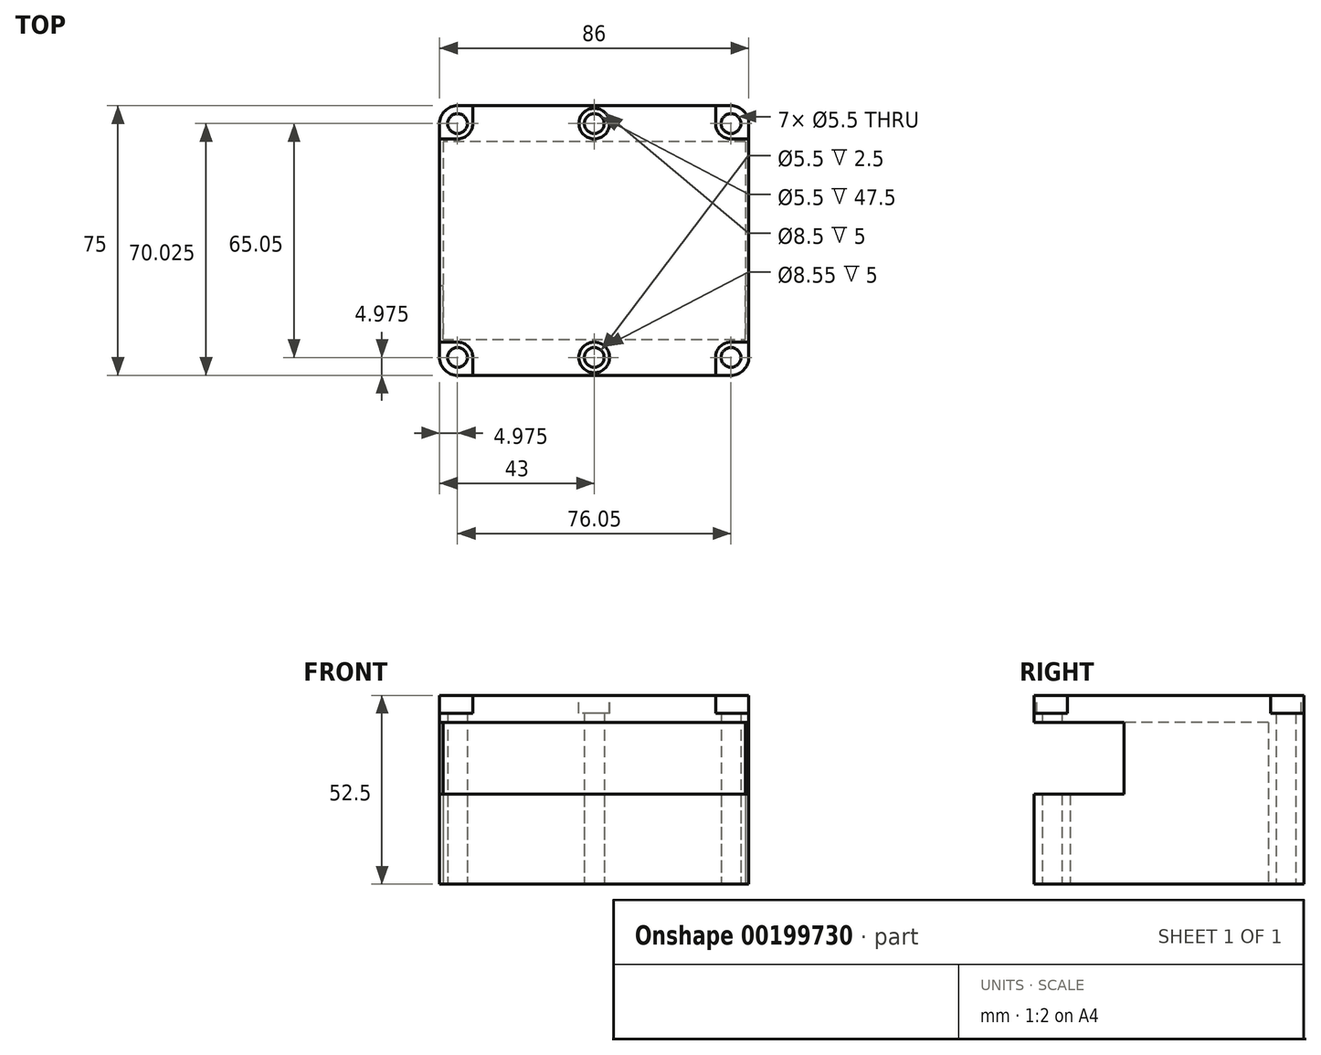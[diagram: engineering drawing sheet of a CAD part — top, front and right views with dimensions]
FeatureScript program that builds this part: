
annotation { "Feature Type Name" : "Feature", "Feature Type Description" : "" }
export const myFeature = defineFeature(function(context is Context, id is Id, definition is map)
    precondition{}
    {
        {
            var Q0;
            Q0=qCreatedBy(makeId("Top.planeOp"),FACE);
            var sketch = newSketch(context, id + "F0", { "sketchPlane" : qUnion([Q0])});
            skLineSegment(sketch, "E0.bottom", {"start": v(42.05, 27.55) * mm, "end": v(-42.05, 27.55) * mm});
            skLineSegment(sketch, "E0.top", {"start": v(42.05, -27.55) * mm, "end": v(-42.05, -27.55) * mm});
            skLineSegment(sketch, "E0.left", {"start": v(42.05, 27.55) * mm, "end": v(42.05, -27.55) * mm});
            skLineSegment(sketch, "E0.right", {"start": v(-42.05, 27.55) * mm, "end": v(-42.05, -27.55) * mm});
            skPoint(sketch, "E0.middle", {"position": v(0, 0) * mm});
            skLineSegment(sketch, "E1.bottom", {"start": v(43, 37.5) * mm, "end": v(-43, 37.5) * mm});
            skLineSegment(sketch, "E1.top", {"start": v(43, -37.5) * mm, "end": v(-43, -37.5) * mm});
            skLineSegment(sketch, "E1.left", {"start": v(43, 37.5) * mm, "end": v(43, -37.5) * mm});
            skLineSegment(sketch, "E1.right", {"start": v(-43, 37.5) * mm, "end": v(-43, -37.5) * mm});
            skSolve(sketch);
        }
        {
            var Q0;
            Q0=makeQuery(id+"F0.imprint","IMPRINT",FACE,{"disambiguationData":[TD([[makeQuery(id+"F0.imprint","IMPRINT",EDGE,{"derivedFrom":sQuery(id+"F0.wireOp",EDGE,"E0.bottom")}),-1.0]])]});
            extrude(context, id + "F1", {"entities" : qUnion([Q0]), "depth" : 45 * mm});
        }
        {
            var Q0;
            Q0=makeQuery(id+"F1.opExtrude","CAP_FACE",FACE,{"disambiguationData":[OSD([sQuery(id+"F0.wireOp",EDGE,"E0.bottom"),sQuery(id+"F0.wireOp",EDGE,"E0.top"),sQuery(id+"F0.wireOp",EDGE,"E0.left"),sQuery(id+"F0.wireOp",EDGE,"E0.right"),sQuery(id+"F0.wireOp",EDGE,"E1.bottom"),sQuery(id+"F0.wireOp",EDGE,"E1.top"),sQuery(id+"F0.wireOp",EDGE,"E1.left"),sQuery(id+"F0.wireOp",EDGE,"E1.right")])],"isStart":false});
            var sketch = newSketch(context, id + "F2", { "sketchPlane" : qUnion([Q0])});
            skLineSegment(sketch, "E2.0.0", {"start": v(43, -37.5) * mm, "end": v(43, 37.5) * mm});
            skLineSegment(sketch, "E2.0.1", {"start": v(43, 37.5) * mm, "end": v(-43, 37.5) * mm});
            skLineSegment(sketch, "E2.0.2", {"start": v(-43, 37.5) * mm, "end": v(-43, -37.5) * mm});
            skLineSegment(sketch, "E2.0.3", {"start": v(-43, -37.5) * mm, "end": v(43, -37.5) * mm});
            skSolve(sketch);
        }
        {
            var Q0;
            Q0=makeQuery(id+"F2.imprint","IMPRINT",FACE,{"disambiguationData":[TD([[makeQuery(id+"F2.imprint","IMPRINT",EDGE,{"derivedFrom":sQuery(id+"F2.wireOp",EDGE,"E2.0.0")}),-1.0]])]});
            var Q1;
            Q1=makeQuery(id+"F2.imprint","IMPRINT",FACE,{"disambiguationData":[TD([[makeQuery(id+"F2.imprint","IMPRINT",EDGE,{"derivedFrom":makeQuery(id+"F1.opExtrude","CAP_EDGE",EDGE,{"disambiguationData":[OSD([sQuery(id+"F0.wireOp",EDGE,"E0.bottom")])],"isStart":false})}),1.0]])]});
            extrude(context, id + "F3", {"entities" : qUnion([Q0, Q1]), "operationType" : NewBodyOperationType.ADD, "depth" : 5 * mm});
        }
        {
            var Q0;
            Q0=makeQuery(id+"F3.boolean.opBoolean","MERGE",FACE,{"derivedFrom":[makeQuery(id+"F1.opExtrude","SWEPT_FACE",FACE,{"disambiguationData":[OSD([sQuery(id+"F0.wireOp",EDGE,"E1.top")])]}),makeQuery(id+"F3.opExtrude","SWEPT_FACE",FACE,{"disambiguationData":[OSD([sQuery(id+"F2.wireOp",EDGE,"E2.0.3")])]})]});
            var sketch = newSketch(context, id + "F4", { "sketchPlane" : qUnion([Q0])});
            skLineSegment(sketch, "E3.0.0", {"start": v(-43, 0) * mm, "end": v(43, 0) * mm});
            skLineSegment(sketch, "E3.0.1", {"start": v(43, 0) * mm, "end": v(43, 50) * mm});
            skLineSegment(sketch, "E3.0.2", {"start": v(43, 50) * mm, "end": v(-43, 50) * mm});
            skLineSegment(sketch, "E3.0.3", {"start": v(-43, 50) * mm, "end": v(-43, 0) * mm});
            skLineSegment(sketch, "E4.bottom", {"start": v(-43, 50) * mm, "end": v(43, 50) * mm});
            skLineSegment(sketch, "E4.top", {"start": v(-43, 25) * mm, "end": v(43, 25) * mm});
            skLineSegment(sketch, "E4.left", {"start": v(-43, 50) * mm, "end": v(-43, 25) * mm});
            skLineSegment(sketch, "E4.right", {"start": v(43, 50) * mm, "end": v(43, 25) * mm});
            skLineSegment(sketch, "E5.top", {"start": v(-43, 45) * mm, "end": v(43, 45) * mm});
            skLineSegment(sketch, "E5.left", {"start": v(-43, 50) * mm, "end": v(-43, 45) * mm});
            skLineSegment(sketch, "E5.right", {"start": v(43, 50) * mm, "end": v(43, 45) * mm});
            skLineSegment(sketch, "E6.bottom", {"start": v(-43, 45) * mm, "end": v(-37.05, 45) * mm});
            skLineSegment(sketch, "E6.top", {"start": v(-43, 25) * mm, "end": v(-37.05, 25) * mm});
            skLineSegment(sketch, "E6.left", {"start": v(-43, 45) * mm, "end": v(-43, 25) * mm});
            skLineSegment(sketch, "E6.right", {"start": v(-37.05, 45) * mm, "end": v(-37.05, 25) * mm});
            skLineSegment(sketch, "E7.bottom", {"start": v(-37.05, 45) * mm, "end": v(-12.05, 45) * mm});
            skLineSegment(sketch, "E7.top", {"start": v(-37.05, 25) * mm, "end": v(-12.05, 25) * mm});
            skLineSegment(sketch, "E7.right", {"start": v(-12.05, 45) * mm, "end": v(-12.05, 25) * mm});
            skLineSegment(sketch, "E8.bottom", {"start": v(-12.05, 45) * mm, "end": v(-10.05, 45) * mm});
            skLineSegment(sketch, "E8.top", {"start": v(-12.05, 25) * mm, "end": v(-10.05, 25) * mm});
            skLineSegment(sketch, "E8.right", {"start": v(-10.05, 45) * mm, "end": v(-10.05, 25) * mm});
            skLineSegment(sketch, "E9.bottom", {"start": v(43, 45) * mm, "end": v(35.95, 45) * mm});
            skLineSegment(sketch, "E9.top", {"start": v(43, 25) * mm, "end": v(35.95, 25) * mm});
            skLineSegment(sketch, "E9.left", {"start": v(43, 45) * mm, "end": v(43, 25) * mm});
            skLineSegment(sketch, "E9.right", {"start": v(35.95, 45) * mm, "end": v(35.95, 25) * mm});
            skSolve(sketch);
        }
        {
            var Q0;
            Q0=makeQuery(id+"F4.imprint","IMPRINT",FACE,{"disambiguationData":[TD([[makeQuery(id+"F4.imprint","IMPRINT",EDGE,{"derivedFrom":sQuery(id+"F4.wireOp",EDGE,"E7.bottom")}),-1.0]])]});
            var Q1;
            Q1=makeQuery(id+"F4.imprint","IMPRINT",FACE,{"disambiguationData":[TD([[makeQuery(id+"F4.imprint","IMPRINT",EDGE,{"derivedFrom":sQuery(id+"F4.wireOp",EDGE,"E4.top")}),1.0]])]});
            extrude(context, id + "F5", {"entities" : qUnion([Q0, Q1]), "operationType" : NewBodyOperationType.REMOVE, "oppositeDirection" : true, "depth" : 25 * mm});
        }
        {
            var Q0;
            Q0=makeQuery(id+"F1.opExtrude","CAP_FACE",FACE,{"disambiguationData":[OSD([sQuery(id+"F0.wireOp",EDGE,"E0.bottom"),sQuery(id+"F0.wireOp",EDGE,"E0.top"),sQuery(id+"F0.wireOp",EDGE,"E0.left"),sQuery(id+"F0.wireOp",EDGE,"E0.right"),sQuery(id+"F0.wireOp",EDGE,"E1.bottom"),sQuery(id+"F0.wireOp",EDGE,"E1.top"),sQuery(id+"F0.wireOp",EDGE,"E1.left"),sQuery(id+"F0.wireOp",EDGE,"E1.right")])],"isStart":true});
            var sketch = newSketch(context, id + "F6", { "sketchPlane" : qUnion([Q0])});
            skLineSegment(sketch, "E10.0.0", {"start": v(43, -37.5) * mm, "end": v(43, 37.5) * mm});
            skLineSegment(sketch, "E10.0.1", {"start": v(43, 37.5) * mm, "end": v(-43, 37.5) * mm});
            skLineSegment(sketch, "E10.0.2", {"start": v(-43, 37.5) * mm, "end": v(-43, -37.5) * mm});
            skLineSegment(sketch, "E10.0.3", {"start": v(-43, -37.5) * mm, "end": v(43, -37.5) * mm});
            skPoint(sketch, "E11", {"position": v(-38.03, -32.52) * mm});
            skPoint(sketch, "E12", {"position": v(38.02, -32.52) * mm});
            skPoint(sketch, "E13", {"position": v(38.03, 32.53) * mm});
            skPoint(sketch, "E14", {"position": v(-38.02, 32.53) * mm});
            skCircle(sketch, "E15", {"center": v(-38.02, 32.53) * mm, "radius": 2.75 * mm});
            skCircle(sketch, "E16", {"center": v(38.03, 32.53) * mm, "radius": 2.75 * mm});
            skCircle(sketch, "E17", {"center": v(-38.03, -32.52) * mm, "radius": 2.75 * mm});
            skCircle(sketch, "E18", {"center": v(38.02, -32.52) * mm, "radius": 2.75 * mm});
            skPoint(sketch, "E19", {"position": v(0, 32.53) * mm});
            skPoint(sketch, "E20", {"position": v(0, -32.52) * mm});
            skCircle(sketch, "E21", {"center": v(0, -32.52) * mm, "radius": 2.75 * mm});
            skCircle(sketch, "E22", {"center": v(0, 32.53) * mm, "radius": 2.75 * mm});
            skSolve(sketch);
        }
        {
            var Q0;
            Q0=makeQuery(id+"F6.imprint","IMPRINT",FACE,{"disambiguationData":[TD([[makeQuery(id+"F6.imprint","IMPRINT",EDGE,{"derivedFrom":sQuery(id+"F6.wireOp",EDGE,"E15")}),1.0]])]});
            var Q1;
            Q1=makeQuery(id+"F6.imprint","IMPRINT",FACE,{"disambiguationData":[TD([[makeQuery(id+"F6.imprint","IMPRINT",EDGE,{"derivedFrom":sQuery(id+"F6.wireOp",EDGE,"E22")}),1.0]])]});
            var Q2;
            Q2=makeQuery(id+"F6.imprint","IMPRINT",FACE,{"disambiguationData":[TD([[makeQuery(id+"F6.imprint","IMPRINT",EDGE,{"derivedFrom":sQuery(id+"F6.wireOp",EDGE,"E16")}),1.0]])]});
            var Q3;
            Q3=makeQuery(id+"F6.imprint","IMPRINT",FACE,{"disambiguationData":[TD([[makeQuery(id+"F6.imprint","IMPRINT",EDGE,{"derivedFrom":sQuery(id+"F6.wireOp",EDGE,"E18")}),1.0]])]});
            var Q4;
            Q4=makeQuery(id+"F6.imprint","IMPRINT",FACE,{"disambiguationData":[TD([[makeQuery(id+"F6.imprint","IMPRINT",EDGE,{"derivedFrom":sQuery(id+"F6.wireOp",EDGE,"E21")}),1.0]])]});
            var Q5;
            Q5=makeQuery(id+"F6.imprint","IMPRINT",FACE,{"disambiguationData":[TD([[makeQuery(id+"F6.imprint","IMPRINT",EDGE,{"derivedFrom":sQuery(id+"F6.wireOp",EDGE,"E17")}),1.0]])]});
            extrude(context, id + "F7", {"entities" : qUnion([Q0, Q1, Q2, Q3, Q4, Q5]), "operationType" : NewBodyOperationType.REMOVE, "endBound" : BoundingType.THROUGH_ALL, "oppositeDirection" : true, "depth" : 25 * mm});
        }
        {
            var Q0;
            Q0=makeQuery(id+"F3.boolean.opBoolean","MERGE",EDGE,{"derivedFrom":[makeQuery(id+"F1.opExtrude","SWEPT_EDGE",EDGE,{"disambiguationData":[OSD([sQuery(id+"F0.wireOp",EDGE,"E1.top"),sQuery(id+"F0.wireOp",EDGE,"E1.left")])]}),makeQuery(id+"F3.opExtrude","SWEPT_EDGE",EDGE,{"disambiguationData":[OSD([sQuery(id+"F2.wireOp",EDGE,"E2.0.0"),sQuery(id+"F2.wireOp",EDGE,"E2.0.3")])]})]});
            var Q1;
            Q1=makeQuery(id+"F3.boolean.opBoolean","MERGE",EDGE,{"derivedFrom":[makeQuery(id+"F1.opExtrude","SWEPT_EDGE",EDGE,{"disambiguationData":[OSD([sQuery(id+"F0.wireOp",EDGE,"E1.bottom"),sQuery(id+"F0.wireOp",EDGE,"E1.left")])]}),makeQuery(id+"F3.opExtrude","SWEPT_EDGE",EDGE,{"disambiguationData":[OSD([sQuery(id+"F2.wireOp",EDGE,"E2.0.0"),sQuery(id+"F2.wireOp",EDGE,"E2.0.1")])]})]});
            var Q2;
            Q2=makeQuery(id+"F3.boolean.opBoolean","MERGE",EDGE,{"derivedFrom":[makeQuery(id+"F1.opExtrude","SWEPT_EDGE",EDGE,{"disambiguationData":[OSD([sQuery(id+"F0.wireOp",EDGE,"E1.bottom"),sQuery(id+"F0.wireOp",EDGE,"E1.right")])]}),makeQuery(id+"F3.opExtrude","SWEPT_EDGE",EDGE,{"disambiguationData":[OSD([sQuery(id+"F2.wireOp",EDGE,"E2.0.1"),sQuery(id+"F2.wireOp",EDGE,"E2.0.2")])]})]});
            var Q3;
            Q3=makeQuery(id+"F3.boolean.opBoolean","MERGE",EDGE,{"derivedFrom":[makeQuery(id+"F1.opExtrude","SWEPT_EDGE",EDGE,{"disambiguationData":[OSD([sQuery(id+"F0.wireOp",EDGE,"E1.top"),sQuery(id+"F0.wireOp",EDGE,"E1.right")])]}),makeQuery(id+"F3.opExtrude","SWEPT_EDGE",EDGE,{"disambiguationData":[OSD([sQuery(id+"F2.wireOp",EDGE,"E2.0.2"),sQuery(id+"F2.wireOp",EDGE,"E2.0.3")])]})]});
            fillet(context, id + "F8", {"entities" : qUnion([Q0, Q1, Q2, Q3]), "radius" : 5 * mm, "tangentPropagation" : true, "allowEdgeOverflow" : false});
        }
        {
            var Q0;
            Q0=makeQuery(id+"F3.opExtrude","CAP_FACE",FACE,{"disambiguationData":[OSD([sQuery(id+"F2.wireOp",EDGE,"E2.0.0"),sQuery(id+"F2.wireOp",EDGE,"E2.0.1"),sQuery(id+"F2.wireOp",EDGE,"E2.0.2"),sQuery(id+"F2.wireOp",EDGE,"E2.0.3")])],"isStart":false});
            var sketch = newSketch(context, id + "F9", { "sketchPlane" : qUnion([Q0])});
            skLineSegment(sketch, "E23.0.0", {"start": v(43, -32.5) * mm, "end": v(43, 32.5) * mm});
            skArc(sketch, "E23.0.1", {"start": v(43, 32.5) * mm, "mid": v(41.54, 36.04) * mm, "end": v(38, 37.5) * mm});
            skLineSegment(sketch, "E23.0.2", {"start": v(38, 37.5) * mm, "end": v(-38, 37.5) * mm});
            skArc(sketch, "E23.0.3", {"start": v(-38, 37.5) * mm, "mid": v(-41.54, 36.04) * mm, "end": v(-43, 32.5) * mm});
            skLineSegment(sketch, "E23.0.4", {"start": v(-43, 32.5) * mm, "end": v(-43, -32.5) * mm});
            skArc(sketch, "E23.0.5", {"start": v(-43, -32.5) * mm, "mid": v(-41.54, -36.04) * mm, "end": v(-38, -37.5) * mm});
            skLineSegment(sketch, "E23.0.6", {"start": v(-38, -37.5) * mm, "end": v(38, -37.5) * mm});
            skArc(sketch, "E23.0.7", {"start": v(38, -37.5) * mm, "mid": v(41.54, -36.04) * mm, "end": v(43, -32.5) * mm});
            skCircle(sketch, "E24", {"center": v(38, -32.5) * mm, "radius": 4.25 * mm});
            skLineSegment(sketch, "E25", {"start": v(33.75, -32.5) * mm, "end": v(33.75, -37.5) * mm});
            skLineSegment(sketch, "E26", {"start": v(38, -28.25) * mm, "end": v(43, -28.25) * mm});
            skCircle(sketch, "E27", {"center": v(38, 32.5) * mm, "radius": 4.25 * mm});
            skCircle(sketch, "E28", {"center": v(-38, 32.5) * mm, "radius": 4.25 * mm});
            skCircle(sketch, "E29", {"center": v(-38, -32.5) * mm, "radius": 4.25 * mm});
            skLineSegment(sketch, "E30", {"start": v(38, 28.25) * mm, "end": v(43, 28.25) * mm});
            skLineSegment(sketch, "E31", {"start": v(33.75, 32.5) * mm, "end": v(33.75, 37.5) * mm});
            skLineSegment(sketch, "E32", {"start": v(-33.75, 32.5) * mm, "end": v(-33.75, 37.5) * mm});
            skLineSegment(sketch, "E33", {"start": v(-38, 28.25) * mm, "end": v(-43, 28.25) * mm});
            skLineSegment(sketch, "E34", {"start": v(-33.75, -32.5) * mm, "end": v(-33.75, -37.5) * mm});
            skLineSegment(sketch, "E35", {"start": v(-38, -28.25) * mm, "end": v(-43, -28.25) * mm});
            skCircle(sketch, "E36", {"center": v(0, -32.53) * mm, "radius": 4.28 * mm});
            skCircle(sketch, "E37", {"center": v(0, 32.52) * mm, "radius": 4.25 * mm});
            skSolve(sketch);
        }
        {
            var Q0;
            {var subQ4=sQuery(id+"F9.wireOp",EDGE,"E23.0.5");Q0=makeQuery(id+"F9.imprint","IMPRINT",FACE,{"disambiguationData":[TD([[makeQuery(id+"F9.imprint","IMPRINT",EDGE,{"derivedFrom":subQ4}),1.0]])]});}
            var Q1;
            {var subQ0=sQuery(id+"F9.wireOp",EDGE,"E29");var subQ1=makeQuery(id+"F9.imprint","INTERSECT",VERTEX,{"derivedFrom":[subQ0,sQuery(id+"F9.wireOp",EDGE,"E34")]});Q1=makeQuery(id+"F9.imprint","IMPRINT",FACE,{"disambiguationData":[TD([[makeQuery(id+"F9.imprint","IMPRINT",EDGE,{"disambiguationData":[TD([[subQ1,-1.0]])],"derivedFrom":subQ0}),1.0]])]});}
            var Q2;
            Q2=makeQuery(id+"F9.imprint","IMPRINT",FACE,{"disambiguationData":[TD([[makeQuery(id+"F9.imprint","IMPRINT",EDGE,{"derivedFrom":sQuery(id+"F9.wireOp",EDGE,"E36")}),1.0]])]});
            var Q3;
            {var subQ0=sQuery(id+"F9.wireOp",EDGE,"E23.0.7");Q3=makeQuery(id+"F9.imprint","IMPRINT",FACE,{"disambiguationData":[TD([[makeQuery(id+"F9.imprint","IMPRINT",EDGE,{"derivedFrom":subQ0}),1.0]])]});}
            var Q4;
            {var subQ0=sQuery(id+"F9.wireOp",EDGE,"E24");var subQ1=makeQuery(id+"F9.imprint","INTERSECT",VERTEX,{"derivedFrom":[subQ0,sQuery(id+"F9.wireOp",EDGE,"E25")]});Q4=makeQuery(id+"F9.imprint","IMPRINT",FACE,{"disambiguationData":[TD([[makeQuery(id+"F9.imprint","IMPRINT",EDGE,{"disambiguationData":[TD([[subQ1,1.0]])],"derivedFrom":subQ0}),1.0]])]});}
            var Q5;
            Q5=makeQuery(id+"F9.imprint","IMPRINT",FACE,{"disambiguationData":[TD([[makeQuery(id+"F9.imprint","IMPRINT",EDGE,{"derivedFrom":sQuery(id+"F9.wireOp",EDGE,"E37")}),1.0]])]});
            var Q6;
            {var subQ1=sQuery(id+"F9.wireOp",EDGE,"E23.0.3");Q6=makeQuery(id+"F9.imprint","IMPRINT",FACE,{"disambiguationData":[TD([[makeQuery(id+"F9.imprint","IMPRINT",EDGE,{"derivedFrom":subQ1}),1.0]])]});}
            var Q7;
            {var subQ0=sQuery(id+"F9.wireOp",EDGE,"E28");var subQ1=makeQuery(id+"F9.imprint","INTERSECT",VERTEX,{"derivedFrom":[subQ0,sQuery(id+"F9.wireOp",EDGE,"E32")]});Q7=makeQuery(id+"F9.imprint","IMPRINT",FACE,{"disambiguationData":[TD([[makeQuery(id+"F9.imprint","IMPRINT",EDGE,{"disambiguationData":[TD([[subQ1,-1.0]])],"derivedFrom":subQ0}),1.0]])]});}
            var Q8;
            {var subQ3=sQuery(id+"F9.wireOp",EDGE,"E23.0.1");Q8=makeQuery(id+"F9.imprint","IMPRINT",FACE,{"disambiguationData":[TD([[makeQuery(id+"F9.imprint","IMPRINT",EDGE,{"derivedFrom":subQ3}),1.0]])]});}
            var Q9;
            {var subQ0=sQuery(id+"F9.wireOp",EDGE,"E27");var subQ1=makeQuery(id+"F9.imprint","INTERSECT",VERTEX,{"derivedFrom":[subQ0,sQuery(id+"F9.wireOp",EDGE,"E30")]});Q9=makeQuery(id+"F9.imprint","IMPRINT",FACE,{"disambiguationData":[TD([[makeQuery(id+"F9.imprint","IMPRINT",EDGE,{"disambiguationData":[TD([[subQ1,1.0]])],"derivedFrom":subQ0}),1.0]])]});}
            extrude(context, id + "F10", {"entities" : qUnion([Q0, Q1, Q2, Q3, Q4, Q5, Q6, Q7, Q8, Q9]), "operationType" : NewBodyOperationType.REMOVE, "oppositeDirection" : true, "depth" : 2.5 * mm});
        }
        {
            var Q0;
            Q0=makeQuery(id+"F3.opExtrude","CAP_FACE",FACE,{"disambiguationData":[OSD([sQuery(id+"F2.wireOp",EDGE,"E2.0.0"),sQuery(id+"F2.wireOp",EDGE,"E2.0.1"),sQuery(id+"F2.wireOp",EDGE,"E2.0.2"),sQuery(id+"F2.wireOp",EDGE,"E2.0.3")])],"isStart":false});
            var sketch = newSketch(context, id + "F11", { "sketchPlane" : qUnion([Q0])});
            skArc(sketch, "E38.0.0", {"start": v(38, 28.25) * mm, "mid": v(35, 29.5) * mm, "end": v(33.75, 32.5) * mm});
            skLineSegment(sketch, "E38.0.1", {"start": v(33.75, 32.5) * mm, "end": v(33.75, 37.5) * mm});
            skLineSegment(sketch, "E38.0.2", {"start": v(33.75, 37.5) * mm, "end": v(-33.75, 37.5) * mm});
            skLineSegment(sketch, "E38.0.3", {"start": v(-33.75, 37.5) * mm, "end": v(-33.75, 32.5) * mm});
            skArc(sketch, "E38.0.4", {"start": v(-33.75, 32.5) * mm, "mid": v(-35, 29.5) * mm, "end": v(-38, 28.25) * mm});
            skLineSegment(sketch, "E38.0.5", {"start": v(-38, 28.25) * mm, "end": v(-43, 28.25) * mm});
            skLineSegment(sketch, "E38.0.6", {"start": v(-43, 28.25) * mm, "end": v(-43, -28.25) * mm});
            skLineSegment(sketch, "E38.0.7", {"start": v(-43, -28.25) * mm, "end": v(-38, -28.25) * mm});
            skArc(sketch, "E38.0.8", {"start": v(-38, -28.25) * mm, "mid": v(-35, -29.5) * mm, "end": v(-33.75, -32.5) * mm});
            skLineSegment(sketch, "E38.0.9", {"start": v(-33.75, -32.5) * mm, "end": v(-33.75, -37.5) * mm});
            skLineSegment(sketch, "E38.0.10", {"start": v(-33.75, -37.5) * mm, "end": v(33.75, -37.5) * mm});
            skLineSegment(sketch, "E38.0.11", {"start": v(33.75, -37.5) * mm, "end": v(33.75, -32.5) * mm});
            skArc(sketch, "E38.0.12", {"start": v(33.75, -32.5) * mm, "mid": v(35, -29.5) * mm, "end": v(38, -28.25) * mm});
            skLineSegment(sketch, "E38.0.13", {"start": v(38, -28.25) * mm, "end": v(43, -28.25) * mm});
            skLineSegment(sketch, "E38.0.14", {"start": v(43, -28.25) * mm, "end": v(43, 28.25) * mm});
            skLineSegment(sketch, "E38.0.15", {"start": v(43, 28.25) * mm, "end": v(38, 28.25) * mm});
            skSolve(sketch);
        }
        {
            var Q0;
            Q0=makeQuery(id+"F11.imprint","IMPRINT",FACE,{"disambiguationData":[TD([[makeQuery(id+"F11.imprint","IMPRINT",EDGE,{"derivedFrom":sQuery(id+"F11.wireOp",EDGE,"E38.0.0")}),-1.0]])]});
            extrude(context, id + "F12", {"entities" : qUnion([Q0]), "operationType" : NewBodyOperationType.ADD, "depth" : 2.5 * mm});
        }
    });
